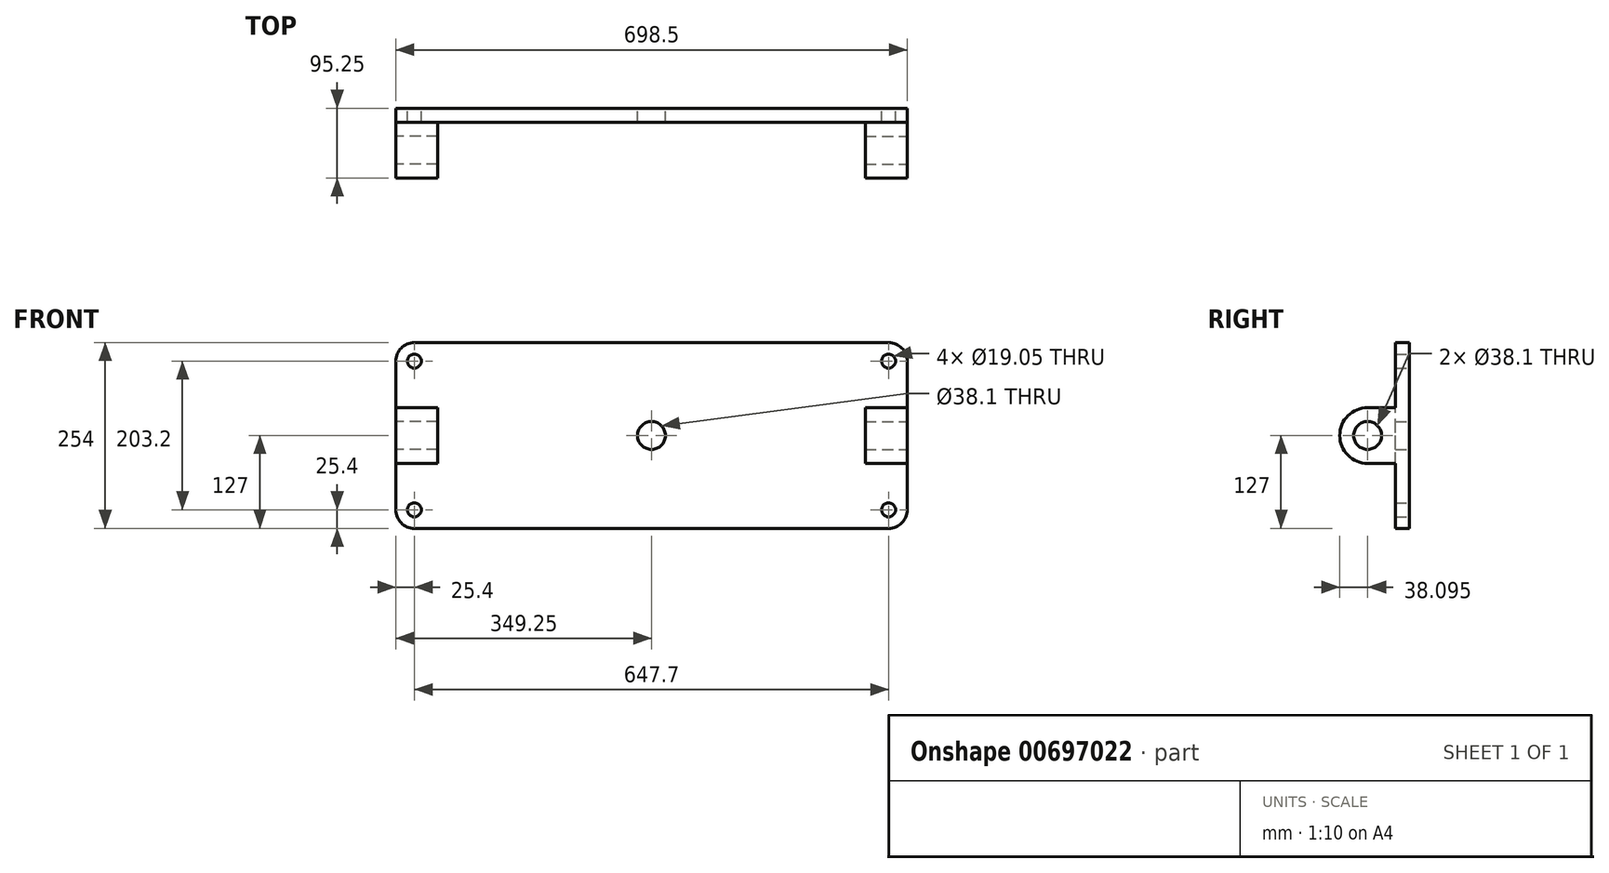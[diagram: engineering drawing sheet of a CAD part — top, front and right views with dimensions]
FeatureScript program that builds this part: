
annotation { "Feature Type Name" : "Feature", "Feature Type Description" : "" }
export const myFeature = defineFeature(function(context is Context, id is Id, definition is map)
    precondition{}
    {
        {
            var Q0;
            Q0=qCreatedBy(makeId("Front.planeOp"),FACE);
            var sketch = newSketch(context, id + "F0", { "sketchPlane" : qUnion([Q0])});
            skLineSegment(sketch, "E0.bottom", {"start": v(323.85, -127) * mm, "end": v(-323.85, -127) * mm});
            skLineSegment(sketch, "E0.top", {"start": v(323.85, 127) * mm, "end": v(-323.85, 127) * mm});
            skLineSegment(sketch, "E0.left", {"start": v(349.25, -101.6) * mm, "end": v(349.25, 101.6) * mm});
            skLineSegment(sketch, "E0.right", {"start": v(-349.25, -101.6) * mm, "end": v(-349.25, 101.6) * mm});
            skPoint(sketch, "E0.middle", {"position": v(0, 0) * mm});
            skLineSegment(sketch, "E1", {"start": v(-349.25, 0) * mm, "end": v(349.25, 0) * mm});
            skLineSegment(sketch, "E2", {"start": v(0, -127) * mm, "end": v(0, 127) * mm});
            skCircle(sketch, "E3", {"center": v(0, 0) * mm, "radius": 19.05 * mm});
            skCircle(sketch, "E4", {"center": v(-323.85, 101.6) * mm, "radius": 9.53 * mm});
            skCircle(sketch, "E5", {"center": v(-323.85, -101.6) * mm, "radius": 9.53 * mm});
            skCircle(sketch, "E6", {"center": v(323.85, 101.6) * mm, "radius": 9.53 * mm});
            skCircle(sketch, "E7", {"center": v(323.85, -101.6) * mm, "radius": 9.53 * mm});
            skPoint(sketch, "E8.visualSharp", {"position": v(-349.25, 127) * mm});
            skArc(sketch, "E8.filletArc", {"start": v(-323.85, 127) * mm, "mid": v(-341.81, 119.56) * mm, "end": v(-349.25, 101.6) * mm});
            skPoint(sketch, "E9.visualSharp", {"position": v(349.25, 127) * mm});
            skArc(sketch, "E9.filletArc", {"start": v(349.25, 101.6) * mm, "mid": v(341.81, 119.56) * mm, "end": v(323.85, 127) * mm});
            skPoint(sketch, "E10.visualSharp", {"position": v(349.25, -127) * mm});
            skArc(sketch, "E10.filletArc", {"start": v(323.85, -127) * mm, "mid": v(341.81, -119.56) * mm, "end": v(349.25, -101.6) * mm});
            skPoint(sketch, "E11.visualSharp", {"position": v(-349.25, -127) * mm});
            skArc(sketch, "E11.filletArc", {"start": v(-349.25, -101.6) * mm, "mid": v(-341.81, -119.56) * mm, "end": v(-323.85, -127) * mm});
            skSolve(sketch);
        }
        {
            var Q0;
            Q0=makeQuery(id+"F0.imprint","IMPRINT",FACE,{"disambiguationData":[TD([[makeQuery(id+"F0.imprint","IMPRINT",EDGE,{"derivedFrom":sQuery(id+"F0.wireOp",EDGE,"E6")}),-1.0]])]});
            var Q1;
            Q1=makeQuery(id+"F0.imprint","IMPRINT",FACE,{"disambiguationData":[TD([[makeQuery(id+"F0.imprint","IMPRINT",EDGE,{"derivedFrom":sQuery(id+"F0.wireOp",EDGE,"E4")}),-1.0]])]});
            var Q2;
            Q2=makeQuery(id+"F0.imprint","IMPRINT",FACE,{"disambiguationData":[TD([[makeQuery(id+"F0.imprint","IMPRINT",EDGE,{"derivedFrom":sQuery(id+"F0.wireOp",EDGE,"E5")}),-1.0]])]});
            var Q3;
            Q3=makeQuery(id+"F0.imprint","IMPRINT",FACE,{"disambiguationData":[TD([[makeQuery(id+"F0.imprint","IMPRINT",EDGE,{"derivedFrom":sQuery(id+"F0.wireOp",EDGE,"E7")}),-1.0]])]});
            extrude(context, id + "F1", {"entities" : qUnion([Q0, Q1, Q2, Q3]), "endBound" : BoundingType.SYMMETRIC, "depth" : 19.05 * mm});
        }
        {
            var Q0;
            Q0=makeQuery(id+"F1.opExtrude","SWEPT_FACE",FACE,{"disambiguationData":[OSD([sQuery(id+"F0.wireOp",EDGE,"E0.left")])]});
            cPlane(context, id + "F2", {"entities" : qUnion([Q0]), "cplaneType" : CPlaneType.OFFSET, "offset" : 0 * mm, "width" : 152.4 * mm, "height" : 152.4 * mm});
        }
        {
            var Q0;
            Q0=qCreatedBy(id+"F2.planeOp",FACE);
            var sketch = newSketch(context, id + "F3", { "sketchPlane" : qUnion([Q0])});
            skLineSegment(sketch, "E12.0", {"start": v(-9.53, -101.6) * mm, "end": v(-9.53, 101.6) * mm});
            skLineSegment(sketch, "E13", {"start": v(-9.53, 0) * mm, "end": v(-47.62, 0) * mm});
            skCircle(sketch, "E14", {"center": v(-47.62, 0) * mm, "radius": 19.05 * mm});
            skCircle(sketch, "E15", {"center": v(-47.62, 0) * mm, "radius": 38.1 * mm});
            skLineSegment(sketch, "E16", {"start": v(-47.62, 38.1) * mm, "end": v(-9.53, 38.1) * mm});
            skLineSegment(sketch, "E17", {"start": v(-47.62, -38.1) * mm, "end": v(-9.53, -38.1) * mm});
            skSolve(sketch);
        }
        {
            var Q0;
            Q0 = qSketchRegion(id + "F3", true);
            extrude(context, id + "F4", {"entities" : qUnion([Q0]), "operationType" : NewBodyOperationType.ADD, "oppositeDirection" : true, "depth" : 57.15 * mm, "offsetDistance" : 25.4 * mm});
        }
        {
            var Q0;
            Q0=makeQuery(id+"F1.opExtrude","SWEPT_FACE",FACE,{"disambiguationData":[OSD([sQuery(id+"F0.wireOp",EDGE,"E0.right")])]});
            cPlane(context, id + "F5", {"entities" : qUnion([Q0]), "cplaneType" : CPlaneType.OFFSET, "offset" : 0 * mm, "width" : 152.4 * mm, "height" : 152.4 * mm});
        }
        {
            var Q0;
            Q0=qCreatedBy(id+"F5.planeOp",FACE);
            var sketch = newSketch(context, id + "F6", { "sketchPlane" : qUnion([Q0])});
            skLineSegment(sketch, "E18.0", {"start": v(9.53, -101.6) * mm, "end": v(9.53, 101.6) * mm});
            skLineSegment(sketch, "E19", {"start": v(9.53, 0) * mm, "end": v(47.62, 0) * mm});
            skCircle(sketch, "E20", {"center": v(47.62, 0) * mm, "radius": 19.05 * mm});
            skCircle(sketch, "E21", {"center": v(47.62, 0) * mm, "radius": 38.1 * mm});
            skLineSegment(sketch, "E22", {"start": v(47.62, 38.1) * mm, "end": v(9.53, 38.1) * mm});
            skLineSegment(sketch, "E23", {"start": v(47.63, -38.1) * mm, "end": v(9.53, -38.1) * mm});
            skSolve(sketch);
        }
        {
            var Q0;
            Q0=makeQuery(id+"F6.imprint","IMPRINT",FACE,{"disambiguationData":[TD([[makeQuery(id+"F6.imprint","IMPRINT",EDGE,{"derivedFrom":sQuery(id+"F6.wireOp",EDGE,"E20")}),-1.0]])]});
            var Q1;
            {var subQ3=sQuery(id+"F6.wireOp",EDGE,"E22");Q1=makeQuery(id+"F6.imprint","IMPRINT",FACE,{"disambiguationData":[TD([[makeQuery(id+"F6.imprint","IMPRINT",EDGE,{"derivedFrom":subQ3}),1.0]])]});}
            var Q2;
            {var subQ3=sQuery(id+"F6.wireOp",EDGE,"E23");Q2=makeQuery(id+"F6.imprint","IMPRINT",FACE,{"disambiguationData":[TD([[makeQuery(id+"F6.imprint","IMPRINT",EDGE,{"derivedFrom":subQ3}),-1.0]])]});}
            extrude(context, id + "F7", {"entities" : qUnion([Q0, Q1, Q2]), "operationType" : NewBodyOperationType.ADD, "oppositeDirection" : true, "depth" : 57.15 * mm, "offsetDistance" : 25.4 * mm});
        }
    });
